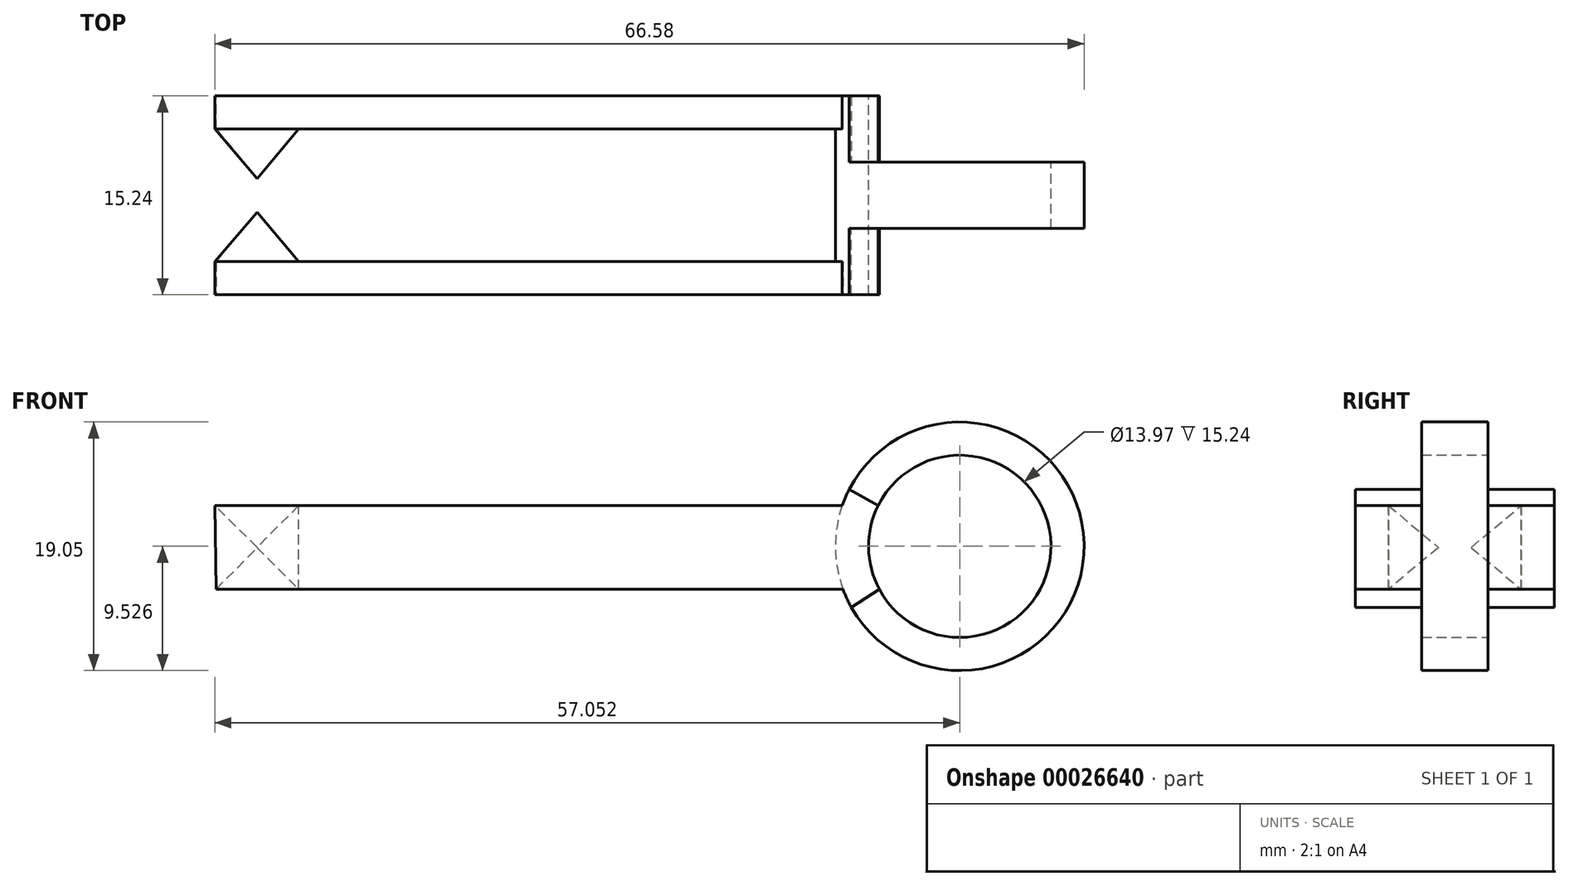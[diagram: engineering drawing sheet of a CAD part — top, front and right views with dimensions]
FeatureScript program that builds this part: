
annotation { "Feature Type Name" : "Feature", "Feature Type Description" : "" }
export const myFeature = defineFeature(function(context is Context, id is Id, definition is map)
    precondition{}
    {
        {
            var Q0;
            Q0=qCreatedBy(makeId("Front.planeOp"),FACE);
            var sketch = newSketch(context, id + "F0", { "sketchPlane" : qUnion([Q0])});
            skCircle(sketch, "E0", {"center": v(-2.83, -7.6) * mm, "radius": 6.99 * mm});
            skCircle(sketch, "E1", {"center": v(-2.83, -7.6) * mm, "radius": 9.53 * mm});
            skSolve(sketch);
        }
        {
            var Q0;
            Q0=makeQuery(id+"F0.imprint","IMPRINT",FACE,{"disambiguationData":[TD([[makeQuery(id+"F0.imprint","IMPRINT",EDGE,{"derivedFrom":sQuery(id+"F0.wireOp",EDGE,"E0")}),-1.0]])]});
            extrude(context, id + "F1", {"entities" : qUnion([Q0]), "depth" : 5.08 * mm});
        }
        {
            var Q0;
            Q0=makeQuery(id+"F1.opExtrude","CAP_FACE",FACE,{"disambiguationData":[OSD([sQuery(id+"F0.wireOp",EDGE,"E0"),sQuery(id+"F0.wireOp",EDGE,"E1")])],"isStart":false});
            var sketch = newSketch(context, id + "F2", { "sketchPlane" : qUnion([Q0])});
            skLineSegment(sketch, "E2", {"start": v(-11.3, -3.23) * mm, "end": v(-9.08, -4.48) * mm});
            skLineSegment(sketch, "E3", {"start": v(-11.12, -12.29) * mm, "end": v(-8.99, -10.9) * mm});
            skSolve(sketch);
        }
        {
            var Q0;
            Q0 = qSketchRegion(id + "F2", true);
            var Q1;
            {var subQ2=sQuery(id+"F2.wireOp",EDGE,"E2");Q1=makeQuery(id+"F2.imprint","IMPRINT",FACE,{"disambiguationData":[TD([[makeQuery(id+"F2.imprint","IMPRINT",EDGE,{"derivedFrom":subQ2}),-1.0]])]});}
            extrude(context, id + "F3", {"entities" : qUnion([Q0, Q1]), "operationType" : NewBodyOperationType.ADD, "depth" : 5.08 * mm});
        }
        {
            var Q0;
            Q0=qCreatedBy(makeId("Front.planeOp"),FACE);
            cPlane(context, id + "F4", {"entities" : qUnion([Q0]), "cplaneType" : CPlaneType.OFFSET, "offset" : 2.54 * mm, "width" : 152.4 * mm, "height" : 152.4 * mm});
        }
        {
            var Q0;
            Q0=makeQuery(id+"F3.opExtrude","CAP_FACE",FACE,{"disambiguationData":[OSD([sQuery(id+"F0.wireOp",EDGE,"E0"),sQuery(id+"F0.wireOp",EDGE,"E1"),sQuery(id+"F2.wireOp",EDGE,"E2"),sQuery(id+"F2.wireOp",EDGE,"E3")])],"isStart":false});
            var sketch = newSketch(context, id + "F5", { "sketchPlane" : qUnion([Q0])});
            skLineSegment(sketch, "E4", {"start": v(-9.08, -4.48) * mm, "end": v(-59.88, -4.48) * mm});
            skLineSegment(sketch, "E5", {"start": v(-8.99, -10.9) * mm, "end": v(-59.79, -10.9) * mm});
            skLineSegment(sketch, "E6", {"start": v(-59.88, -4.48) * mm, "end": v(-59.79, -10.9) * mm});
            skSolve(sketch);
        }
        {
            var Q0;
            {var subQ5=sQuery(id+"F5.wireOp",EDGE,"E6");Q0=makeQuery(id+"F5.imprint","IMPRINT",FACE,{"disambiguationData":[TD([[makeQuery(id+"F5.imprint","IMPRINT",EDGE,{"derivedFrom":subQ5}),1.0]])]});}
            extrude(context, id + "F6", {"entities" : qUnion([Q0]), "operationType" : NewBodyOperationType.ADD, "oppositeDirection" : true, "depth" : 2.54 * mm});
        }
        {
            var Q0;
            Q0=makeQuery(id+"F6.opExtrude","CAP_FACE",FACE,{"disambiguationData":[OSD([sQuery(id+"F0.wireOp",EDGE,"E1"),sQuery(id+"F5.wireOp",EDGE,"E4"),sQuery(id+"F5.wireOp",EDGE,"E5"),sQuery(id+"F5.wireOp",EDGE,"E6")])],"isStart":false});
            var sketch = newSketch(context, id + "F7", { "sketchPlane" : qUnion([Q0])});
            skLineSegment(sketch, "E7", {"start": v(53.45, -4.48) * mm, "end": v(53.45, -10.9) * mm});
            skLineSegment(sketch, "E8", {"start": v(53.45, -4.48) * mm, "end": v(59.88, -4.48) * mm});
            skLineSegment(sketch, "E9", {"start": v(59.79, -10.9) * mm, "end": v(53.45, -4.48) * mm});
            skLineSegment(sketch, "E10", {"start": v(53.45, -10.9) * mm, "end": v(59.88, -4.48) * mm});
            skPoint(sketch, "E11", {"position": v(56.64, -7.71) * mm});
            skSolve(sketch);
        }
        {
            var Q0;
            {var subQ3=sQuery(id+"F7.wireOp",EDGE,"E8");Q0=makeQuery(id+"F7.imprint","IMPRINT",FACE,{"disambiguationData":[TD([[makeQuery(id+"F7.imprint","IMPRINT",EDGE,{"derivedFrom":subQ3}),-1.0]])]});}
            var Q1;
            {var subQ3=sQuery(id+"F7.wireOp",EDGE,"E7");Q1=makeQuery(id+"F7.imprint","IMPRINT",FACE,{"disambiguationData":[TD([[makeQuery(id+"F7.imprint","IMPRINT",EDGE,{"derivedFrom":subQ3}),1.0]])]});}
            var Q2;
            {var subQ1=sQuery(id+"F7.wireOp",EDGE,"E10");var subQ3=sQuery(id+"F7.wireOp",EDGE,"E9");var subQ5=makeQuery(id+"F7.imprint","INTERSECT",VERTEX,{"derivedFrom":[subQ3,subQ1]});Q2=makeQuery(id+"F7.imprint","IMPRINT",FACE,{"disambiguationData":[TD([[makeQuery(id+"F7.imprint","IMPRINT",EDGE,{"disambiguationData":[TD([[subQ5,1.0]])],"derivedFrom":subQ3}),1.0]])]});}
            var Q3;
            {var subQ0=makeQuery(id+"F6.opExtrude","CAP_EDGE",EDGE,{"disambiguationData":[OSD([sQuery(id+"F5.wireOp",EDGE,"E6")])],"isStart":false});Q3=makeQuery(id+"F7.imprint","IMPRINT",FACE,{"disambiguationData":[TD([[makeQuery(id+"F7.imprint","IMPRINT",EDGE,{"derivedFrom":subQ0}),-1.0]])]});}
            extrude(context, id + "F8", {"entities" : qUnion([Q0, Q1, Q2, Q3]), "operationType" : NewBodyOperationType.ADD, "depth" : 5.08 * mm, "hasDraft" : true, "draftAngle" : 40 * degree, "draftPullDirection" : true});
        }
        {
            var Q0;
            Q0=makeQuery(id+"F1.opExtrude","SWEPT_BODY",BODY,{"disambiguationData":[OSD([sQuery(id+"F0.wireOp",EDGE,"E0"),sQuery(id+"F0.wireOp",EDGE,"E1")])]});
            var Q1;
            Q1=makeQuery(id+"F8.opExtrude","SWEPT_BODY",BODY,{"disambiguationData":[OSD([sQuery(id+"F5.wireOp",EDGE,"E5"),sQuery(id+"F5.wireOp",EDGE,"E6"),sQuery(id+"F7.wireOp",EDGE,"E7"),sQuery(id+"F7.wireOp",EDGE,"E8")])]});
            var Q2;
            Q2=qCreatedBy(id+"F4.planeOp",FACE);
            mirror(context, id + "F9", {"operationType" : NewBodyOperationType.ADD, "entities" : qUnion([Q0, Q1]), "mirrorPlane" : qUnion([Q2])});
        }
    });
